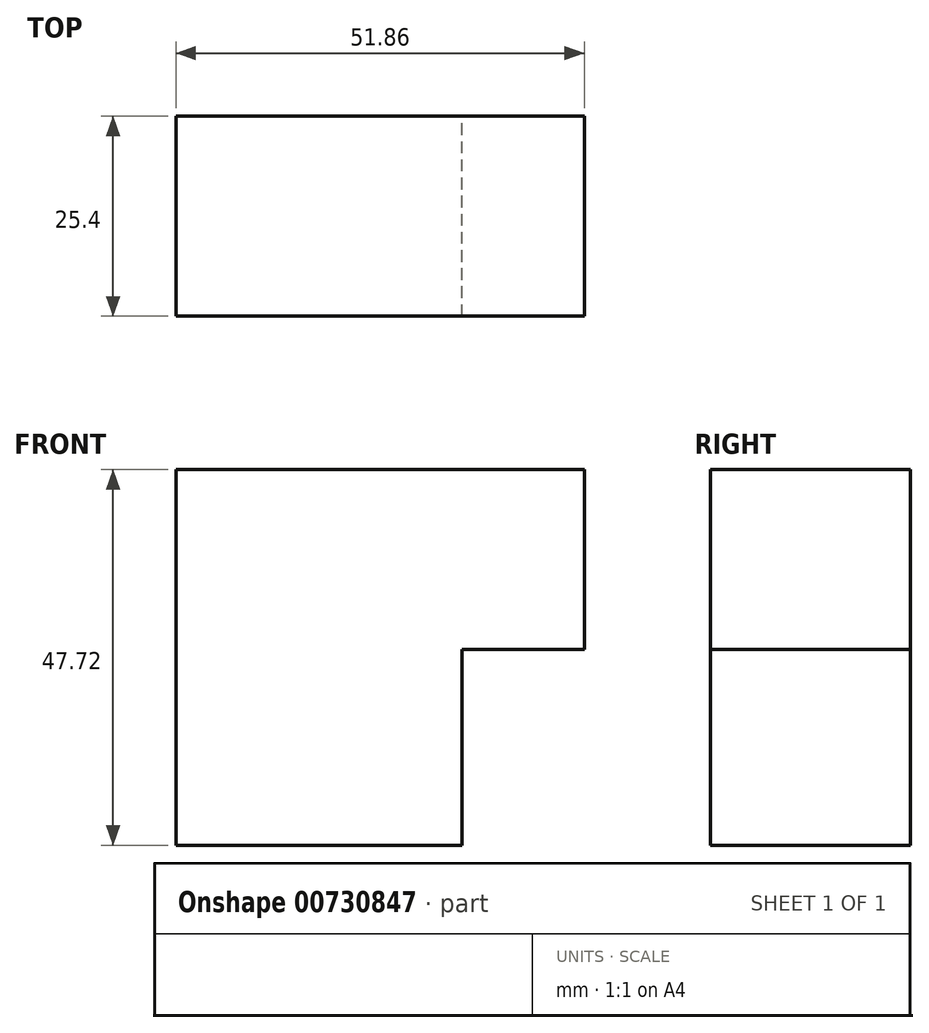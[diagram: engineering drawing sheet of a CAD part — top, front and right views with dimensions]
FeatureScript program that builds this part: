
annotation { "Feature Type Name" : "Feature", "Feature Type Description" : "" }
export const myFeature = defineFeature(function(context is Context, id is Id, definition is map)
    precondition{}
    {
        {
            var Q0;
            Q0=qCreatedBy(makeId("Front.planeOp"),FACE);
            var sketch = newSketch(context, id + "F0", { "sketchPlane" : qUnion([Q0])});
            skLineSegment(sketch, "E0.bottom", {"start": v(-14.31, 47.72) * mm, "end": v(51.86, 47.72) * mm});
            skLineSegment(sketch, "E0.top", {"start": v(-14.31, -23.44) * mm, "end": v(51.86, -23.44) * mm});
            skLineSegment(sketch, "E0.left", {"start": v(-14.31, 47.72) * mm, "end": v(-14.31, -23.44) * mm});
            skLineSegment(sketch, "E0.right", {"start": v(51.86, 47.72) * mm, "end": v(51.86, -23.44) * mm});
            skLineSegment(sketch, "E1.bottom", {"start": v(18.77, 47.72) * mm, "end": v(30.5, 47.72) * mm});
            skLineSegment(sketch, "E1.top", {"start": v(18.77, 47.72) * mm, "end": v(30.5, 47.72) * mm});
            skLineSegment(sketch, "E1.left", {"start": v(18.77, 47.72) * mm, "end": v(18.77, 47.72) * mm});
            skLineSegment(sketch, "E1.right", {"start": v(30.5, 47.72) * mm, "end": v(30.5, 47.72) * mm});
            skLineSegment(sketch, "E2.bottom", {"start": v(51.86, 24.9) * mm, "end": v(0, 24.9) * mm});
            skLineSegment(sketch, "E2.top", {"start": v(51.86, 47.72) * mm, "end": v(0, 47.72) * mm});
            skLineSegment(sketch, "E2.left", {"start": v(51.86, 24.9) * mm, "end": v(51.86, 47.72) * mm});
            skLineSegment(sketch, "E2.right", {"start": v(0, 24.9) * mm, "end": v(0, 47.72) * mm});
            skLineSegment(sketch, "E3.bottom", {"start": v(36.3, 0) * mm, "end": v(0, 0) * mm});
            skLineSegment(sketch, "E3.top", {"start": v(36.3, 24.9) * mm, "end": v(0, 24.9) * mm});
            skLineSegment(sketch, "E3.left", {"start": v(36.3, 0) * mm, "end": v(36.3, 24.9) * mm});
            skLineSegment(sketch, "E3.right", {"start": v(0, 0) * mm, "end": v(0, 24.9) * mm});
            skSolve(sketch);
        }
        {
            var Q0;
            Q0=makeQuery(id+"F0.imprint","IMPRINT",FACE,{"disambiguationData":[TD([[makeQuery(id+"F0.imprint","IMPRINT",EDGE,{"derivedFrom":sQuery(id+"F0.wireOp",EDGE,"E3.bottom")}),-1.0]])]});
            var Q1;
            Q1=makeQuery(id+"F0.imprint","IMPRINT",FACE,{"disambiguationData":[TD([[makeQuery(id+"F0.imprint","IMPRINT",EDGE,{"derivedFrom":sQuery(id+"F0.wireOp",EDGE,"E0.bottom")}),-1.0]])]});
            var Q2;
            Q2=makeQuery(id+"F0.imprint","IMPRINT",FACE,{"disambiguationData":[TD([[makeQuery(id+"F0.imprint","IMPRINT",EDGE,{"derivedFrom":sQuery(id+"F0.wireOp",EDGE,"E2.bottom")}),-1.0]])]});
            extrude(context, id + "F1", {"entities" : qUnion([Q0, Q1, Q2]), "depth" : 25.4 * mm, "offsetDistance" : 25.4 * mm});
        }
    });
